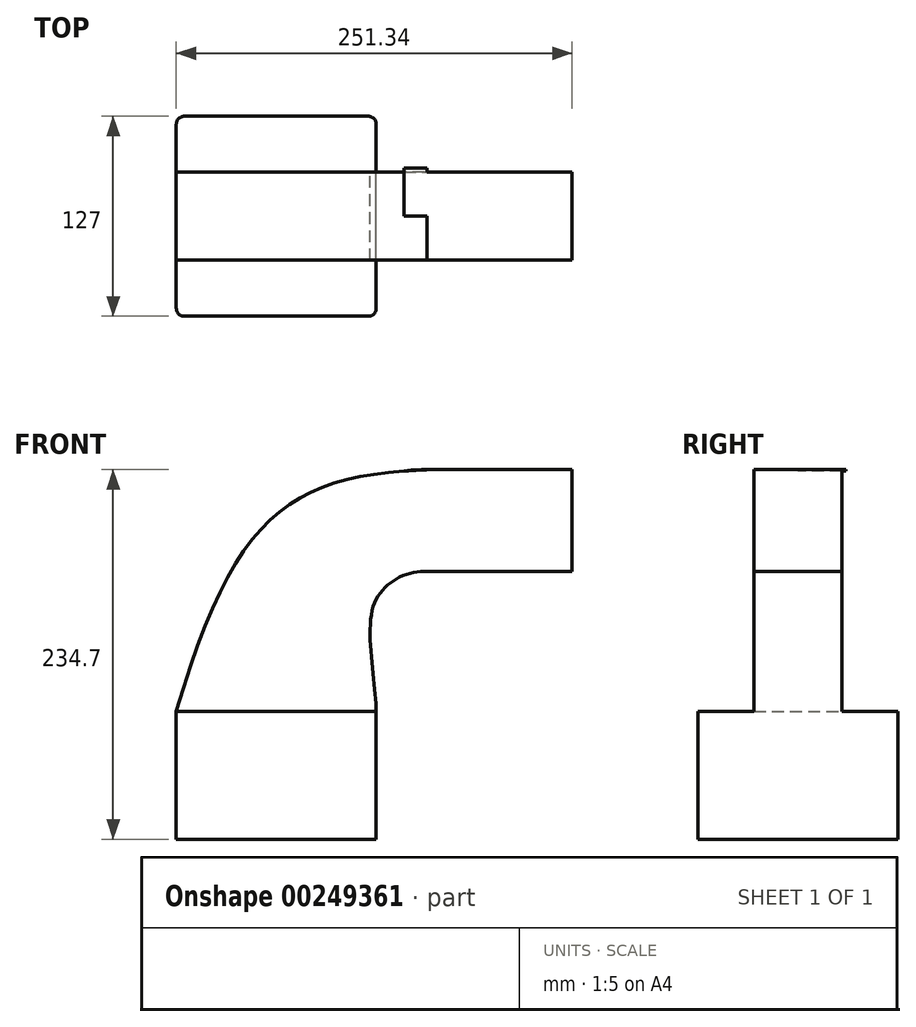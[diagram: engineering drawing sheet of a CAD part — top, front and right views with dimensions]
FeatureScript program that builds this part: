
annotation { "Feature Type Name" : "Feature", "Feature Type Description" : "" }
export const myFeature = defineFeature(function(context is Context, id is Id, definition is map)
    precondition{}
    {
        {
            var Q0;
            Q0=qCreatedBy(makeId("Front.planeOp"),FACE);
            var sketch = newSketch(context, id + "F0", { "sketchPlane" : qUnion([Q0])});
            skLineSegment(sketch, "E0.bottom", {"start": v(63.5, -40.64) * mm, "end": v(-63.5, -40.64) * mm});
            skLineSegment(sketch, "E0.top", {"start": v(63.5, 40.64) * mm, "end": v(-63.5, 40.64) * mm});
            skLineSegment(sketch, "E0.left", {"start": v(63.5, -40.64) * mm, "end": v(63.5, 40.64) * mm});
            skLineSegment(sketch, "E0.right", {"start": v(-63.5, -40.64) * mm, "end": v(-63.5, 40.64) * mm});
            skPoint(sketch, "E0.middle", {"position": v(0, 0) * mm});
            skLineSegment(sketch, "E1.bottom", {"start": v(243.72, 126.24) * mm, "end": v(187.84, 126.24) * mm});
            skLineSegment(sketch, "E1.top", {"start": v(243.72, 197.36) * mm, "end": v(187.84, 197.36) * mm});
            skLineSegment(sketch, "E1.left", {"start": v(243.72, 126.24) * mm, "end": v(243.72, 197.36) * mm});
            skLineSegment(sketch, "E1.right", {"start": v(187.84, 126.24) * mm, "end": v(187.84, 197.36) * mm});
            skPoint(sketch, "E1.middle", {"position": v(215.78, 161.8) * mm});
            skFitSpline(sketch, "E2", {"points": [v(63.5, 40.64) * mm, v(63.5, 111.7) * mm], "startDerivative": vector(0, 53.22) * mm, "endDerivative": vector(26.26, 46.3) * mm});
            skArc(sketch, "E3", {"start": v(63.5, 111.7) * mm, "mid": v(76.4, 124.76) * mm, "end": v(94.12, 129.54) * mm});
            skLineSegment(sketch, "E4", {"start": v(94.12, 129.54) * mm, "end": v(216.04, 129.54) * mm});
            skLineSegment(sketch, "E5.0", {"start": v(94.12, 194.06) * mm, "end": v(215.51, 194.06) * mm});
            skArc(sketch, "E5.1", {"start": v(7.38, 143.53) * mm, "mid": v(43.93, 180.5) * mm, "end": v(94.12, 194.06) * mm});
            skFitSpline(sketch, "E5.2", {"points": [v(-1, 40) * mm, v(-1, 40.04) * mm, v(-1, 40.1) * mm, v(-1, 40.22) * mm, v(-1.01, 40.3) * mm, v(-1.01, 40.38) * mm, v(-1.01, 40.42) * mm, v(-1.01, 40.46) * mm, v(-1.01, 40.48) * mm, v(-1.01, 40.5) * mm, v(-1.02, 40.53) * mm, v(-1.02, 40.54) * mm, v(-1.02, 40.55) * mm, v(-1.02, 40.55) * mm, v(-1.02, 40.55) * mm, v(-1.02, 40.55) * mm, v(-1.02, 40.55) * mm, v(-1.02, 40.55) * mm, v(-1.02, 40.55) * mm, v(-1.02, 40.55) * mm, v(-1.02, 40.56) * mm, v(-1.02, 40.57) * mm, v(-1.02, 40.6) * mm, v(-1.02, 40.65) * mm, v(-1.02, 40.75) * mm, v(-1.03, 40.87) * mm, v(-1.03, 41.02) * mm, v(-1.05, 41.24) * mm, v(-1.07, 41.59) * mm, v(-1.1, 42.25) * mm, v(-1.19, 43.26) * mm, v(-1.32, 44.75) * mm, v(-1.49, 46.48) * mm, v(-1.69, 48.4) * mm, v(-1.91, 50.51) * mm, v(-2.17, 52.79) * mm, v(-2.53, 56.02) * mm, v(-3, 60.4) * mm, v(-3.6, 66.11) * mm, v(-4.14, 72.25) * mm, v(-4.6, 78.78) * mm, v(-4.9, 85.74) * mm, v(-4.94, 93.16) * mm, v(-4.63, 101.15) * mm, v(-3.9, 108.44) * mm, v(-2.89, 114.78) * mm, v(-1.84, 119.82) * mm, v(-0.42, 125.2) * mm, v(1.47, 130.93) * mm, v(3.96, 137.03) * mm, v(6.13, 141.33) * mm, v(7.38, 143.53) * mm]});
            skLineSegment(sketch, "E6", {"start": v(215.51, 194.06) * mm, "end": v(216.04, 129.54) * mm});
            skFitSpline(sketch, "E7", {"points": [v(-63.5, 40.64) * mm, v(215.51, 194.06) * mm], "startDerivative": vector(151.14, 516.68) * mm, "endDerivative": vector(544, 0) * mm});
            skSolve(sketch);
        }
        {
            var Q0;
            Q0=makeQuery(id+"F0.imprint","IMPRINT",FACE,{"disambiguationData":[TD([[makeQuery(id+"F0.imprint","IMPRINT",EDGE,{"derivedFrom":sQuery(id+"F0.wireOp",EDGE,"E0.bottom")}),-1.0]])]});
            extrude(context, id + "F1", {"entities" : qUnion([Q0]), "endBound" : BoundingType.SYMMETRIC, "depth" : 127 * mm});
        }
        {
            var Q0;
            {var subQ1=sQuery(id+"F0.wireOp",EDGE,"E2");Q0=makeQuery(id+"F0.imprint","IMPRINT",FACE,{"disambiguationData":[TD([[makeQuery(id+"F0.imprint","IMPRINT",EDGE,{"derivedFrom":subQ1}),1.0]])]});}
            extrude(context, id + "F2", {"entities" : qUnion([Q0]), "operationType" : NewBodyOperationType.ADD, "endBound" : BoundingType.SYMMETRIC, "depth" : 55.88 * mm});
        }
        {
            var Q0;
            {var subQ5=sQuery(id+"F0.wireOp",EDGE,"E5.1");Q0=makeQuery(id+"F0.imprint","IMPRINT",FACE,{"disambiguationData":[TD([[makeQuery(id+"F0.imprint","IMPRINT",EDGE,{"derivedFrom":subQ5}),1.0]])]});}
            extrude(context, id + "F3", {"entities" : qUnion([Q0]), "operationType" : NewBodyOperationType.ADD, "oppositeDirection" : true, "depth" : 30.48 * mm});
        }
        {
            var Q0;
            Q0=sQuery(id+"F0.wireOp",EDGE,"E1.left");
            var Q1;
            Q1=sQuery(id+"F0.wireOp",EDGE,"E1.top");
            var Q2;
            Q2=sQuery(id+"F0.wireOp",EDGE,"E1.bottom");
            var Q3;
            Q3=sQuery(id+"F0.wireOp",EDGE,"E1.right");
            revolve(context, id + "F4", {"bodyType" : ToolBodyType.SURFACE, "surfaceEntities" : qUnion([Q0, Q1, Q2]), "axis" : qUnion([Q3]), "revolveType" : RevolveType.FULL});
        }
        {
            var Q0;
            Q0=makeQuery(id+"F1.opExtrude","CAP_EDGE",EDGE,{"disambiguationData":[OSD([sQuery(id+"F0.wireOp",EDGE,"E0.right")])],"isStart":false});
            var Q1;
            Q1=makeQuery(id+"F1.opExtrude","CAP_EDGE",EDGE,{"disambiguationData":[OSD([sQuery(id+"F0.wireOp",EDGE,"E0.left")])],"isStart":false});
            var Q2;
            Q2=makeQuery(id+"F1.opExtrude","CAP_EDGE",EDGE,{"disambiguationData":[OSD([sQuery(id+"F0.wireOp",EDGE,"E0.left")])],"isStart":true});
            var Q3;
            Q3=makeQuery(id+"F1.opExtrude","CAP_EDGE",EDGE,{"disambiguationData":[OSD([sQuery(id+"F0.wireOp",EDGE,"E0.right")])],"isStart":true});
            fillet(context, id + "F5", {"entities" : qUnion([Q0, Q1, Q2, Q3]), "radius" : 5.08 * mm, "tangentPropagation" : true, "allowEdgeOverflow" : false});
        }
    });
